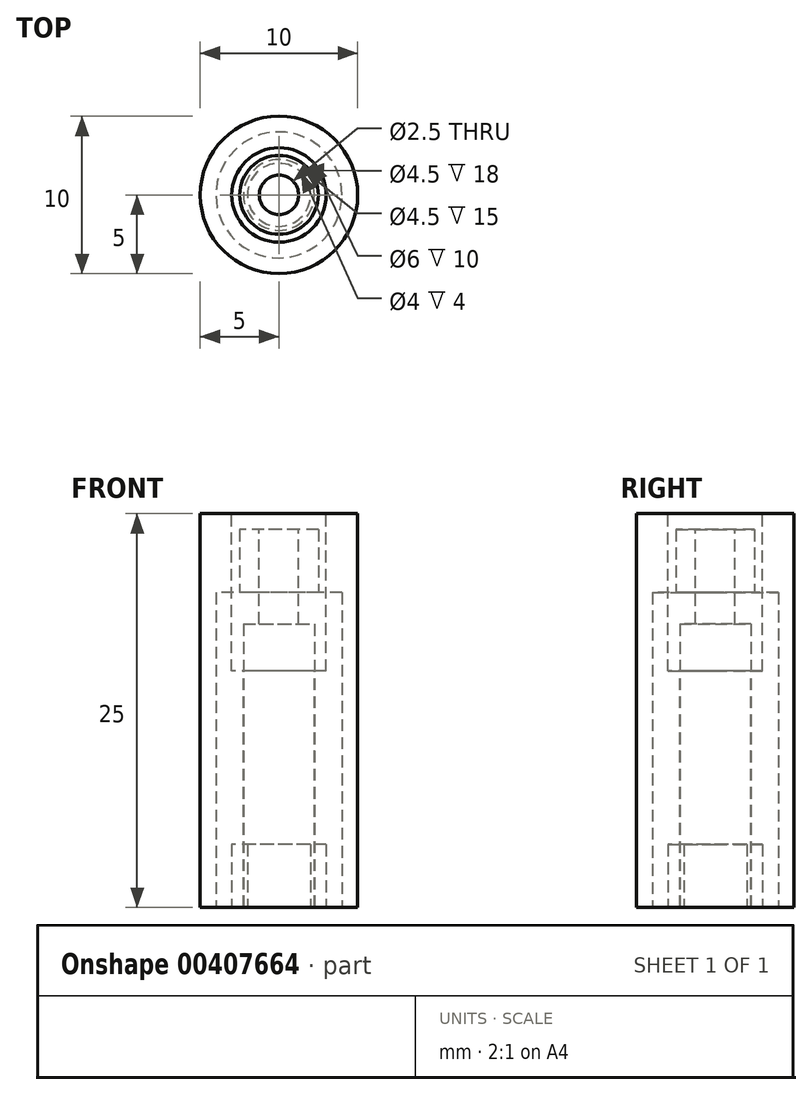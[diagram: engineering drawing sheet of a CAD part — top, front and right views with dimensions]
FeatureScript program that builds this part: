
annotation { "Feature Type Name" : "Feature", "Feature Type Description" : "" }
export const myFeature = defineFeature(function(context is Context, id is Id, definition is map)
    precondition{}
    {
        {
            var Q0;
            Q0=qCreatedBy(makeId("Top.planeOp"),FACE);
            var sketch = newSketch(context, id + "F0", { "sketchPlane" : qUnion([Q0])});
            skCircle(sketch, "E0", {"center": v(0, 0) * mm, "radius": 5 * mm});
            skSolve(sketch);
        }
        {
            var Q0;
            Q0 = qSketchRegion(id + "F0", true);
            extrude(context, id + "F1", {"entities" : qUnion([Q0]), "depth" : 25 * mm});
        }
        {
            var Q0;
            Q0=makeQuery(id+"F1.opExtrude","CAP_FACE",FACE,{"disambiguationData":[OSD([sQuery(id+"F0.wireOp",EDGE,"E0")])],"isStart":false});
            var sketch = newSketch(context, id + "F2", { "sketchPlane" : qUnion([Q0])});
            skCircle(sketch, "E1", {"center": v(0, 0) * mm, "radius": 2.25 * mm});
            skSolve(sketch);
        }
        {
            var Q0;
            Q0 = qSketchRegion(id + "F2", true);
            extrude(context, id + "F3", {"entities" : qUnion([Q0]), "operationType" : NewBodyOperationType.REMOVE, "endBound" : BoundingType.THROUGH_ALL, "oppositeDirection" : true, "depth" : 25 * mm});
        }
        {
            var Q0;
            Q0=makeQuery(id+"F1.opExtrude","CAP_FACE",FACE,{"disambiguationData":[OSD([sQuery(id+"F0.wireOp",EDGE,"E0")])],"isStart":false});
            var sketch = newSketch(context, id + "F4", { "sketchPlane" : qUnion([Q0])});
            skCircle(sketch, "E2", {"center": v(0, 0) * mm, "radius": 3 * mm});
            skSolve(sketch);
        }
        {
            var Q0;
            Q0 = qSketchRegion(id + "F4", true);
            extrude(context, id + "F5", {"entities" : qUnion([Q0]), "operationType" : NewBodyOperationType.REMOVE, "oppositeDirection" : true, "depth" : 10 * mm});
        }
        {
            var Q0;
            Q0=qCreatedBy(makeId("Top.planeOp"),FACE);
            var sketch = newSketch(context, id + "F6", { "sketchPlane" : qUnion([Q0])});
            skCircle(sketch, "E3", {"center": v(0, 0) * mm, "radius": 4 * mm});
            skSolve(sketch);
        }
        {
            var Q0;
            Q0=makeQuery(id+"F6.imprint","IMPRINT",FACE,{"disambiguationData":[TD([[makeQuery(id+"F6.imprint","IMPRINT",EDGE,{"derivedFrom":sQuery(id+"F6.wireOp",EDGE,"E3")}),1.0]])]});
            extrude(context, id + "F7", {"entities" : qUnion([Q0]), "depth" : 20 * mm});
        }
        {
            var Q0;
            Q0=makeQuery(id+"F7.opExtrude","CAP_FACE",FACE,{"disambiguationData":[OSD([sQuery(id+"F6.wireOp",EDGE,"E3")])],"isStart":false});
            var sketch = newSketch(context, id + "F8", { "sketchPlane" : qUnion([Q0])});
            skCircle(sketch, "E4", {"center": v(0, 0) * mm, "radius": 2.5 * mm});
            skSolve(sketch);
        }
        {
            var Q0;
            Q0 = qSketchRegion(id + "F8", true);
            extrude(context, id + "F9", {"entities" : qUnion([Q0]), "operationType" : NewBodyOperationType.ADD, "depth" : 4 * mm});
        }
        {
            var Q0;
            Q0=makeQuery(id+"F9.opExtrude","CAP_FACE",FACE,{"disambiguationData":[OSD([sQuery(id+"F8.wireOp",EDGE,"E4")])],"isStart":false});
            var sketch = newSketch(context, id + "F10", { "sketchPlane" : qUnion([Q0])});
            skCircle(sketch, "E5", {"center": v(0, 0) * mm, "radius": 1.25 * mm});
            skSolve(sketch);
        }
        {
            var Q0;
            Q0 = qSketchRegion(id + "F10", true);
            extrude(context, id + "F11", {"entities" : qUnion([Q0]), "operationType" : NewBodyOperationType.REMOVE, "endBound" : BoundingType.THROUGH_ALL, "oppositeDirection" : true, "depth" : 25 * mm});
        }
        {
            var Q0;
            Q0=makeQuery(id+"F7.opExtrude","CAP_FACE",FACE,{"disambiguationData":[OSD([sQuery(id+"F6.wireOp",EDGE,"E3")])],"isStart":true});
            var sketch = newSketch(context, id + "F12", { "sketchPlane" : qUnion([Q0])});
            skCircle(sketch, "E6", {"center": v(0, 0) * mm, "radius": 2.25 * mm});
            skSolve(sketch);
        }
        {
            var Q0;
            Q0 = qSketchRegion(id + "F12", true);
            extrude(context, id + "F13", {"entities" : qUnion([Q0]), "operationType" : NewBodyOperationType.REMOVE, "oppositeDirection" : true, "depth" : 18 * mm});
        }
        {
            var Q0;
            Q0=qCreatedBy(makeId("Top.planeOp"),FACE);
            var sketch = newSketch(context, id + "F14", { "sketchPlane" : qUnion([Q0])});
            skCircle(sketch, "E7", {"center": v(0, 0) * mm, "radius": 2 * mm});
            skCircle(sketch, "E8", {"center": v(0, 0) * mm, "radius": 3 * mm});
            skSolve(sketch);
        }
        {
            var Q0;
            Q0 = qSketchRegion(id + "F14", true);
            extrude(context, id + "F15", {"entities" : qUnion([Q0]), "depth" : 4 * mm});
        }
    });
